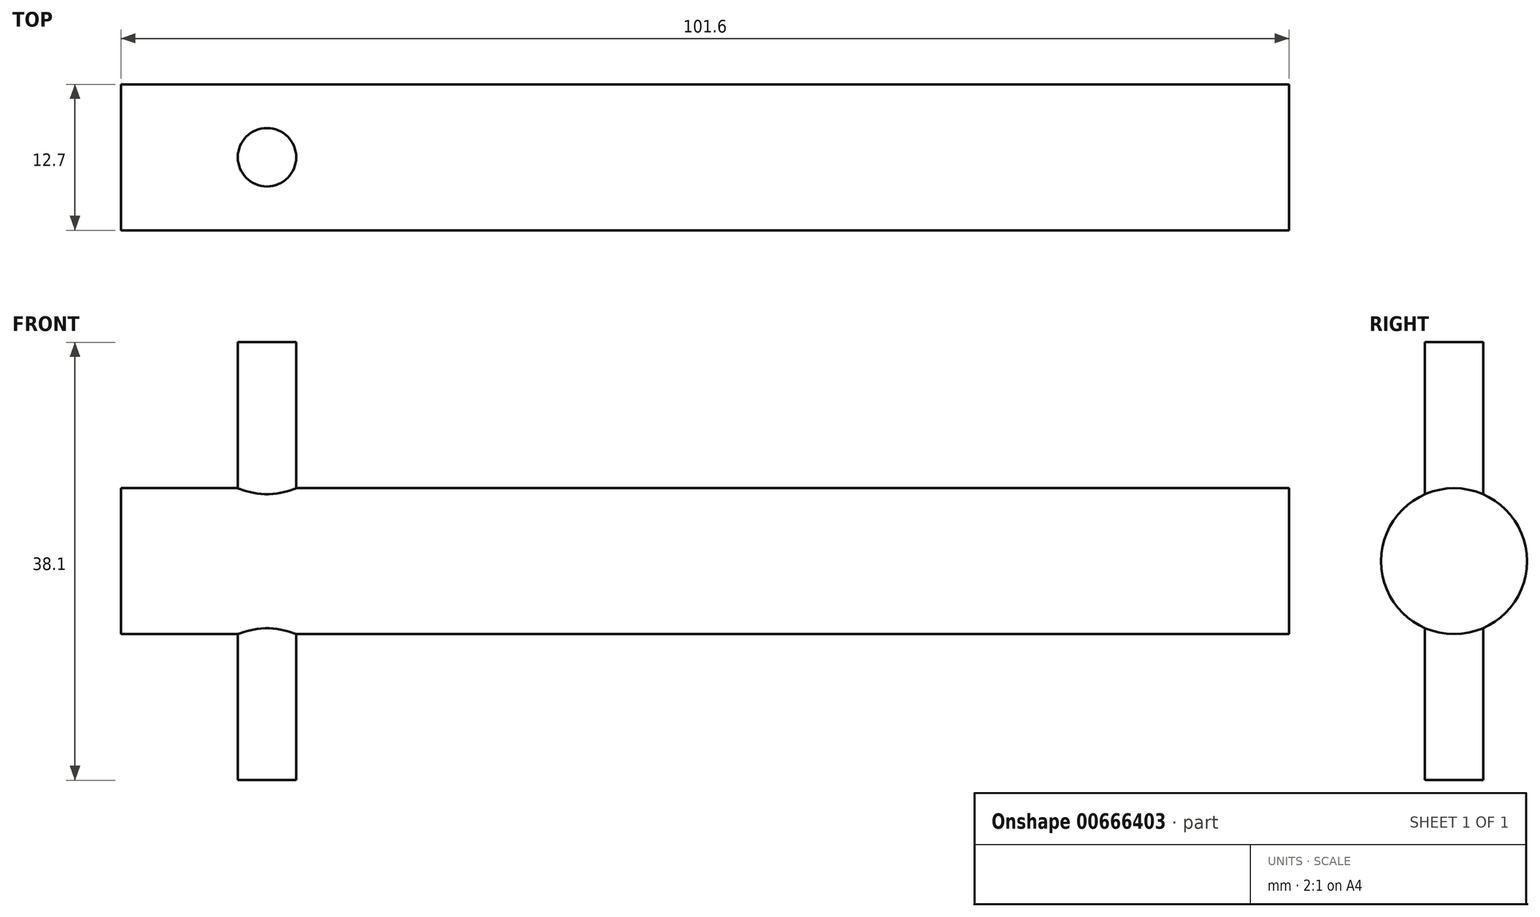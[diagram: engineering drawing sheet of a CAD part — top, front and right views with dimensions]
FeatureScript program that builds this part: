
annotation { "Feature Type Name" : "Feature", "Feature Type Description" : "" }
export const myFeature = defineFeature(function(context is Context, id is Id, definition is map)
    precondition{}
    {
        {
            var Q0;
            Q0=qCreatedBy(makeId("Right.planeOp"),FACE);
            var sketch = newSketch(context, id + "F0", { "sketchPlane" : qUnion([Q0])});
            skLineSegment(sketch, "E0.bottom", {"start": v(-7.43, 8.4) * mm, "end": v(5.27, 8.4) * mm});
            skLineSegment(sketch, "E0.top", {"start": v(-7.43, 21.1) * mm, "end": v(5.27, 21.1) * mm});
            skLineSegment(sketch, "E0.left", {"start": v(-7.43, 8.4) * mm, "end": v(-7.43, 21.1) * mm});
            skLineSegment(sketch, "E0.right", {"start": v(5.27, 8.4) * mm, "end": v(5.27, 21.1) * mm});
            skSolve(sketch);
        }
        {
            var Q0;
            Q0 = qSketchRegion(id + "F0", true);
            extrude(context, id + "F1", {"entities" : qUnion([Q0]), "depth" : 101.6 * mm, "offsetDistance" : 25.4 * mm});
        }
        {
            var Q0;
            Q0=makeQuery(id+"F1.opExtrude","SWEPT_FACE",FACE,{"disambiguationData":[OSD([sQuery(id+"F0.wireOp",EDGE,"E0.top")])]});
            var sketch = newSketch(context, id + "F2", { "sketchPlane" : qUnion([Q0])});
            skCircle(sketch, "E1", {"center": v(12.7, -1.08) * mm, "radius": 2.54 * mm});
            skSolve(sketch);
        }
        {
            var Q0;
            Q0 = qSketchRegion(id + "F2", true);
            extrude(context, id + "F3", {"entities" : qUnion([Q0]), "operationType" : NewBodyOperationType.ADD, "oppositeDirection" : true, "depth" : 25.4 * mm, "offsetDistance" : 25.4 * mm});
        }
        {
            var Q0;
            Q0 = qSketchRegion(id + "F2", true);
            extrude(context, id + "F4", {"entities" : qUnion([Q0]), "operationType" : NewBodyOperationType.ADD, "depth" : 12.7 * mm, "offsetDistance" : 25.4 * mm});
        }
        {
            var Q0;
            Q0=makeQuery(id+"F1.opExtrude","SWEPT_EDGE",EDGE,{"disambiguationData":[OSD([sQuery(id+"F0.wireOp",EDGE,"E0.top"),sQuery(id+"F0.wireOp",EDGE,"E0.left")])]});
            var Q1;
            Q1=makeQuery(id+"F1.opExtrude","SWEPT_EDGE",EDGE,{"disambiguationData":[OSD([sQuery(id+"F0.wireOp",EDGE,"E0.top"),sQuery(id+"F0.wireOp",EDGE,"E0.right")])]});
            var Q2;
            Q2=makeQuery(id+"F1.opExtrude","SWEPT_EDGE",EDGE,{"disambiguationData":[OSD([sQuery(id+"F0.wireOp",EDGE,"E0.bottom"),sQuery(id+"F0.wireOp",EDGE,"E0.left")])]});
            var Q3;
            Q3=makeQuery(id+"F1.opExtrude","SWEPT_EDGE",EDGE,{"disambiguationData":[OSD([sQuery(id+"F0.wireOp",EDGE,"E0.bottom"),sQuery(id+"F0.wireOp",EDGE,"E0.right")])]});
            fillet(context, id + "F5", {"entities" : qUnion([Q0, Q1, Q2, Q3]), "radius" : 6.35 * mm, "tangentPropagation" : true, "allowEdgeOverflow" : false});
        }
    });
